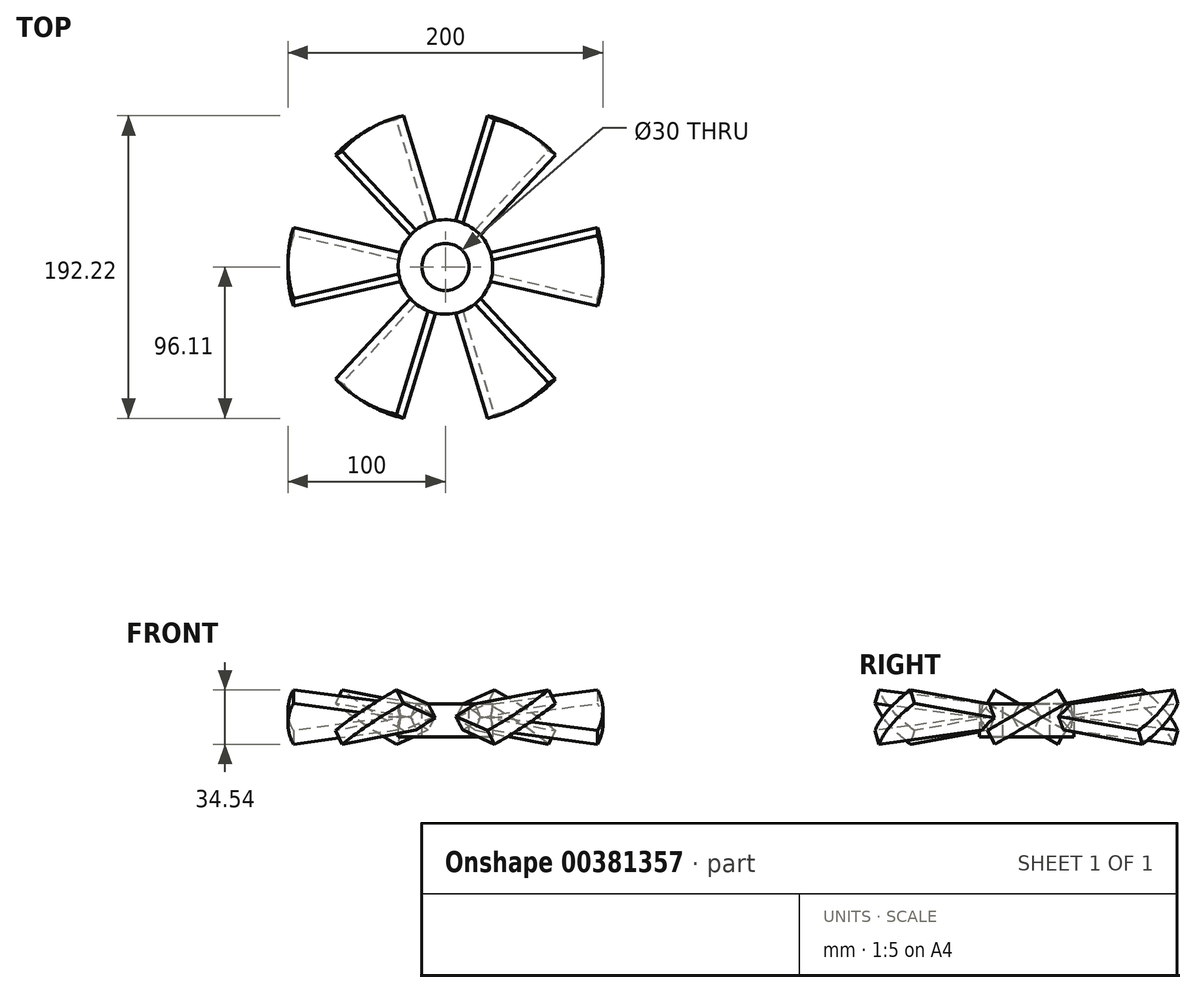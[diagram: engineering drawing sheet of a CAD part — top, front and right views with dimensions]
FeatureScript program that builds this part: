
annotation { "Feature Type Name" : "Feature", "Feature Type Description" : "" }
export const myFeature = defineFeature(function(context is Context, id is Id, definition is map)
    precondition{}
    {
        {
            var Q0;
            Q0=qCreatedBy(makeId("Top.planeOp"),FACE);
            var sketch = newSketch(context, id + "F0", { "sketchPlane" : qUnion([Q0])});
            skLineSegment(sketch, "E0", {"start": v(0, 0) * mm, "end": v(85.68, 0) * mm, "construction": true});
            skLineSegment(sketch, "E1", {"start": v(0, 0) * mm, "end": v(96.6, -25.88) * mm});
            skArc(sketch, "E2", {"start": v(96.6, -25.88) * mm, "mid": v(100, 0) * mm, "end": v(96.6, 25.88) * mm});
            skLineSegment(sketch, "E3.MirrorCS", {"start": v(0, 0) * mm, "end": v(96.6, 25.88) * mm});
            skSolve(sketch);
        }
        {
            var Q0;
            Q0=makeQuery(id+"F0.imprint","IMPRINT",FACE,{"disambiguationData":[TD([[makeQuery(id+"F0.imprint","IMPRINT",EDGE,{"derivedFrom":sQuery(id+"F0.wireOp",EDGE,"E1")}),1.0]])]});
            extrude(context, id + "F1", {"entities" : qUnion([Q0]), "endBound" : BoundingType.SYMMETRIC, "depth" : 10 * mm});
        }
        {
            var Q0;
            Q0=qCreatedBy(makeId("Top.planeOp"),FACE);
            var sketch = newSketch(context, id + "F2", { "sketchPlane" : qUnion([Q0])});
            skLineSegment(sketch, "E4", {"start": v(-38.16, 0) * mm, "end": v(0, 0) * mm, "construction": true});
            skSolve(sketch);
        }
        {
            var Q0;
            Q0=makeQuery(id+"F1.opExtrude","SWEPT_BODY",BODY,{"disambiguationData":[OSD([sQuery(id+"F0.wireOp",EDGE,"E1"),sQuery(id+"F0.wireOp",EDGE,"E2"),sQuery(id+"F0.wireOp",EDGE,"E3.MirrorCS")])]});
            var Q1;
            Q1=sQuery(id+"F2.wireOp",EDGE,"E4");
            transform(context, id + "F3", {"entities" : qUnion([Q0]), "transformType" : TransformType.ROTATION, "transformAxis" : qUnion([Q1]), "angle" : 30 * degree, "makeCopy" : false});
        }
        {
            var Q0;
            Q0=qCreatedBy(makeId("Front.planeOp"),FACE);
            var sketch = newSketch(context, id + "F4", { "sketchPlane" : qUnion([Q0])});
            skLineSegment(sketch, "E5", {"start": v(0, 0) * mm, "end": v(0, 34.53) * mm, "construction": true});
            skSolve(sketch);
        }
        {
            var Q0;
            Q0=makeQuery(id+"F1.opExtrude","SWEPT_BODY",BODY,{"disambiguationData":[OSD([sQuery(id+"F0.wireOp",EDGE,"E1"),sQuery(id+"F0.wireOp",EDGE,"E2"),sQuery(id+"F0.wireOp",EDGE,"E3.MirrorCS")])]});
            var Q1;
            Q1=sQuery(id+"F4.wireOp",EDGE,"E5");
            circularPattern(context, id + "F5", {"entities" : qUnion([Q0]), "axis" : qUnion([Q1]), "angle" : 360 * degree, "instanceCount" : 6, "equalSpace" : true});
        }
        {
            var Q0;
            Q0=qCreatedBy(makeId("Top.planeOp"),FACE);
            var sketch = newSketch(context, id + "F6", { "sketchPlane" : qUnion([Q0])});
            skCircle(sketch, "E6", {"center": v(0, 0) * mm, "radius": 30 * mm});
            skSolve(sketch);
        }
        {
            var Q0;
            Q0=makeQuery(id+"F6.imprint","IMPRINT",FACE,{"disambiguationData":[TD([[makeQuery(id+"F6.imprint","IMPRINT",EDGE,{"derivedFrom":sQuery(id+"F6.wireOp",EDGE,"E6")}),1.0]])]});
            extrude(context, id + "F7", {"entities" : qUnion([Q0]), "endBound" : BoundingType.SYMMETRIC, "depth" : 25 * mm});
        }
        {
            var Q0;
            Q0=makeQuery(id+"F1.opExtrude","SWEPT_BODY",BODY,{"disambiguationData":[OSD([sQuery(id+"F0.wireOp",EDGE,"E1"),sQuery(id+"F0.wireOp",EDGE,"E2"),sQuery(id+"F0.wireOp",EDGE,"E3.MirrorCS")])]});
            var Q1;
            Q1=makeQuery(id+"F5.opPattern","COPY",BODY,{"derivedFrom":makeQuery(id+"F1.opExtrude","SWEPT_BODY",BODY,{"disambiguationData":[OSD([sQuery(id+"F0.wireOp",EDGE,"E1"),sQuery(id+"F0.wireOp",EDGE,"E2"),sQuery(id+"F0.wireOp",EDGE,"E3.MirrorCS")])]}),"instanceName":"1"});
            var Q2;
            Q2=makeQuery(id+"F5.opPattern","COPY",BODY,{"derivedFrom":makeQuery(id+"F1.opExtrude","SWEPT_BODY",BODY,{"disambiguationData":[OSD([sQuery(id+"F0.wireOp",EDGE,"E1"),sQuery(id+"F0.wireOp",EDGE,"E2"),sQuery(id+"F0.wireOp",EDGE,"E3.MirrorCS")])]}),"instanceName":"2"});
            var Q3;
            Q3=makeQuery(id+"F5.opPattern","COPY",BODY,{"derivedFrom":makeQuery(id+"F1.opExtrude","SWEPT_BODY",BODY,{"disambiguationData":[OSD([sQuery(id+"F0.wireOp",EDGE,"E1"),sQuery(id+"F0.wireOp",EDGE,"E2"),sQuery(id+"F0.wireOp",EDGE,"E3.MirrorCS")])]}),"instanceName":"3"});
            var Q4;
            Q4=makeQuery(id+"F5.opPattern","COPY",BODY,{"derivedFrom":makeQuery(id+"F1.opExtrude","SWEPT_BODY",BODY,{"disambiguationData":[OSD([sQuery(id+"F0.wireOp",EDGE,"E1"),sQuery(id+"F0.wireOp",EDGE,"E2"),sQuery(id+"F0.wireOp",EDGE,"E3.MirrorCS")])]}),"instanceName":"4"});
            var Q5;
            Q5=makeQuery(id+"F5.opPattern","COPY",BODY,{"derivedFrom":makeQuery(id+"F1.opExtrude","SWEPT_BODY",BODY,{"disambiguationData":[OSD([sQuery(id+"F0.wireOp",EDGE,"E1"),sQuery(id+"F0.wireOp",EDGE,"E2"),sQuery(id+"F0.wireOp",EDGE,"E3.MirrorCS")])]}),"instanceName":"5"});
            var Q6;
            Q6=makeQuery(id+"F7.opExtrude","SWEPT_BODY",BODY,{"disambiguationData":[OSD([sQuery(id+"F6.wireOp",EDGE,"E6")])]});
            booleanBodies(context, id + "F8", {"operationType" : BooleanOperationType.UNION, "tools" : qUnion([Q0, Q1, Q2, Q3, Q4, Q5, Q6])});
        }
        {
            var Q0;
            {var subQ0=sQuery(id+"F0.wireOp",EDGE,"E3.MirrorCS");Q0=makeQuery(id+"F8.opBoolean","INTERSECT",VERTEX,{"derivedFrom":[makeQuery(id+"F5.opPattern","COPY",FACE,{"derivedFrom":makeQuery(id+"F1.opExtrude","CAP_FACE",FACE,{"disambiguationData":[OSD([sQuery(id+"F0.wireOp",EDGE,"E1"),sQuery(id+"F0.wireOp",EDGE,"E2"),subQ0])],"isStart":false}),"instanceName":"4"}),makeQuery(id+"F5.opPattern","COPY",FACE,{"derivedFrom":makeQuery(id+"F1.opExtrude","SWEPT_FACE",FACE,{"disambiguationData":[OSD([subQ0])]}),"instanceName":"4"}),makeQuery(id+"F7.opExtrude","SWEPT_FACE",FACE,{"disambiguationData":[OSD([sQuery(id+"F6.wireOp",EDGE,"E6")])]})]});}
            var Q1;
            {var subQ0=sQuery(id+"F0.wireOp",EDGE,"E3.MirrorCS");Q1=makeQuery(id+"F8.opBoolean","INTERSECT",VERTEX,{"derivedFrom":[makeQuery(id+"F5.opPattern","COPY",FACE,{"derivedFrom":makeQuery(id+"F1.opExtrude","CAP_FACE",FACE,{"disambiguationData":[OSD([sQuery(id+"F0.wireOp",EDGE,"E1"),sQuery(id+"F0.wireOp",EDGE,"E2"),subQ0])],"isStart":false}),"instanceName":"5"}),makeQuery(id+"F5.opPattern","COPY",FACE,{"derivedFrom":makeQuery(id+"F1.opExtrude","SWEPT_FACE",FACE,{"disambiguationData":[OSD([subQ0])]}),"instanceName":"5"}),makeQuery(id+"F7.opExtrude","SWEPT_FACE",FACE,{"disambiguationData":[OSD([sQuery(id+"F6.wireOp",EDGE,"E6")])]})]});}
            var Q2;
            {var subQ0=sQuery(id+"F0.wireOp",EDGE,"E3.MirrorCS");Q2=makeQuery(id+"F8.opBoolean","INTERSECT",VERTEX,{"derivedFrom":[makeQuery(id+"F1.opExtrude","CAP_FACE",FACE,{"disambiguationData":[OSD([sQuery(id+"F0.wireOp",EDGE,"E1"),sQuery(id+"F0.wireOp",EDGE,"E2"),subQ0])],"isStart":false}),makeQuery(id+"F1.opExtrude","SWEPT_FACE",FACE,{"disambiguationData":[OSD([subQ0])]}),makeQuery(id+"F7.opExtrude","SWEPT_FACE",FACE,{"disambiguationData":[OSD([sQuery(id+"F6.wireOp",EDGE,"E6")])]})]});}
            cPlane(context, id + "F9", {"entities" : qUnion([Q0, Q1, Q2]), "cplaneType" : CPlaneType.THREE_POINT, "offset" : 25 * mm, "width" : 150 * mm, "height" : 150 * mm});
        }
        {
            var Q0;
            Q0=makeQuery(id+"F7.opExtrude","CAP_FACE",FACE,{"disambiguationData":[OSD([sQuery(id+"F6.wireOp",EDGE,"E6")])],"isStart":false});
            var Q1;
            Q1=qCreatedBy(id+"F9.planeOp",FACE);
            extrude(context, id + "F10", {"entities" : qUnion([Q0]), "operationType" : NewBodyOperationType.REMOVE, "endBound" : BoundingType.UP_TO_SURFACE, "oppositeDirection" : true, "endBoundEntityFace" : qUnion([Q1]), "depth" : 25 * mm});
        }
        {
            var Q0;
            Q0=makeQuery(id+"F10.boolean.opBoolean","COPY",FACE,{"derivedFrom":makeQuery(id+"F10.opExtrude","CAP_FACE",FACE,{"disambiguationData":[OSD([sQuery(id+"F6.wireOp",EDGE,"E6")])],"isStart":false})});
            var sketch = newSketch(context, id + "F11", { "sketchPlane" : qUnion([Q0])});
            skCircle(sketch, "E7", {"center": v(0, 0) * mm, "radius": 15 * mm});
            skSolve(sketch);
        }
        {
            var Q0;
            Q0 = qSketchRegion(id + "F11", true);
            extrude(context, id + "F12", {"entities" : qUnion([Q0]), "operationType" : NewBodyOperationType.REMOVE, "endBound" : BoundingType.THROUGH_ALL, "oppositeDirection" : true, "depth" : 25 * mm});
        }
    });
